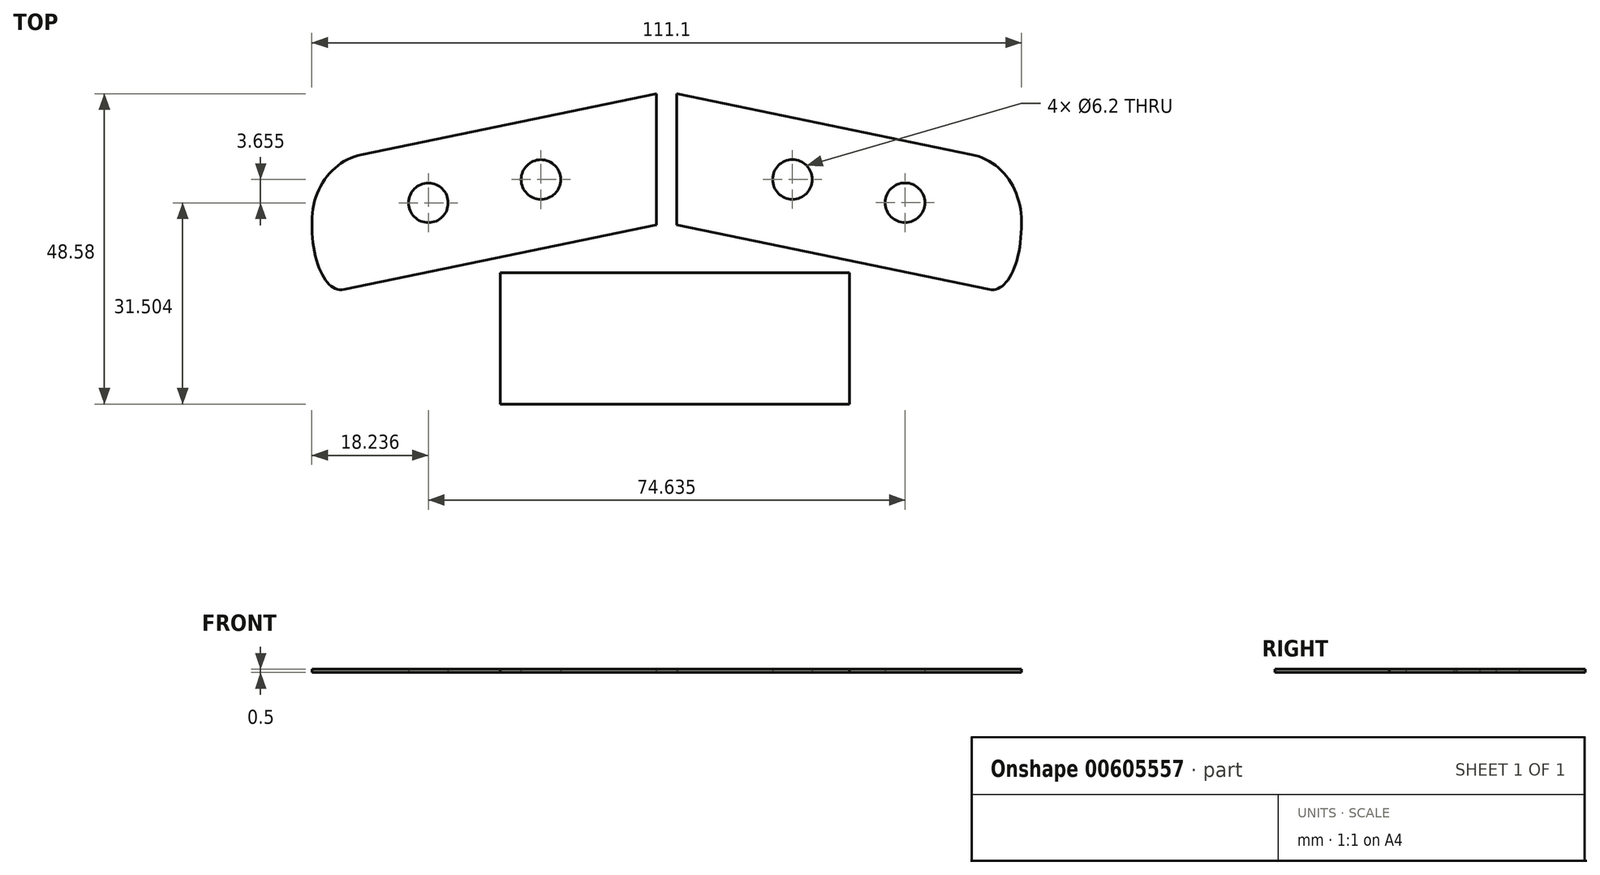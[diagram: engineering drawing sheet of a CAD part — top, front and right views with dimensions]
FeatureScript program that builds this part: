
annotation { "Feature Type Name" : "Feature", "Feature Type Description" : "" }
export const myFeature = defineFeature(function(context is Context, id is Id, definition is map)
    precondition{}
    {
        {
            var Q0;
            Q0=qCreatedBy(makeId("Top.planeOp"),FACE);
            var sketch = newSketch(context, id + "F0", { "sketchPlane" : qUnion([Q0])});
            skLineSegment(sketch, "E0.0", {"start": v(-43.66, 1.52) * mm, "end": v(-43.66, 22.05) * mm});
            skLineSegment(sketch, "E0.1", {"start": v(-43.66, 1.52) * mm, "end": v(11, 1.52) * mm});
            skLineSegment(sketch, "E0.2", {"start": v(-43.66, 22.05) * mm, "end": v(11, 22.05) * mm});
            skLineSegment(sketch, "E0.3", {"start": v(11, 22.05) * mm, "end": v(11, 1.52) * mm});
            skLineSegment(sketch, "E1.0", {"start": v(-16, 50.1) * mm, "end": v(-16, 29.57) * mm});
            skLineSegment(sketch, "E1.1", {"start": v(32.93, 19.46) * mm, "end": v(-16, 29.57) * mm});
            skLineSegment(sketch, "E1.2", {"start": v(30.16, 40.58) * mm, "end": v(-15.93, 50.1) * mm});
            skCircle(sketch, "E1.3", {"center": v(2.1, 36.68) * mm, "radius": 3.1 * mm});
            skCircle(sketch, "E1.4", {"center": v(19.72, 33.04) * mm, "radius": 3.1 * mm});
            skEllipticalArc(sketch, "E1.5", {});
            skEllipticalArc(sketch, "E1.6", {});
            skLineSegment(sketch, "E1.7", {"start": v(37.95, 30.13) * mm, "end": v(37.95, 29.84) * mm});
            skLineSegment(sketch, "E2.0", {"start": v(-16, 50.1) * mm, "end": v(-15.93, 50.1) * mm});
            skLineSegment(sketch, "E3.0", {"start": v(-19.2, 29.55) * mm, "end": v(-19.2, 50.08) * mm});
            skLineSegment(sketch, "E3.1", {"start": v(-68.12, 19.45) * mm, "end": v(-19.2, 29.55) * mm});
            skCircle(sketch, "E3.2", {"center": v(-54.91, 33.02) * mm, "radius": 3.1 * mm});
            skCircle(sketch, "E3.3", {"center": v(-37.29, 36.66) * mm, "radius": 3.1 * mm});
            skLineSegment(sketch, "E3.4", {"start": v(-65.36, 40.57) * mm, "end": v(-19.27, 50.09) * mm});
            skLineSegment(sketch, "E3.5", {"start": v(-19.27, 50.09) * mm, "end": v(-19.2, 50.08) * mm});
            skEllipticalArc(sketch, "E3.6", {});
            skEllipticalArc(sketch, "E3.7", {});
            skLineSegment(sketch, "E3.8", {"start": v(-73.15, 30.11) * mm, "end": v(-73.15, 29.83) * mm});
            const initialGuessF0  = {"E1.5": [0.03292744071812428, 0.030879444010317995, -0.04895262450957913, 0.9988011015981232, 0.011474428753066477, 0.005, 3.0295878582004208, 4.600384184987563], "E1.6": [0.02790194554591465, 0.029633939155095018, 0.2022282773088944, 0.9793384113046302, 0.011180339887498943, 0.01, 4.939281783143953, 0], "E3.6": [-0.06309490990535518, 0.029619057740934936, -0.20222827730889414, 0.9793384113046303, 0.011180339887498943, 0.01, 0, 1.343903524035634], "E3.7": [-0.06812040507756481, 0.030864562596157767, -0.048952624509578754, -0.9988011015981231, 0.01147442875306648, 0.005, 4.8243937757811715, 0.11200479537014071]};
            skSetInitialGuess(sketch, initialGuessF0);
            skSolve(sketch);
        }
        {
            var Q0;
            Q0 = qSketchRegion(id + "F0", true);
            extrude(context, id + "F1", {"entities" : qUnion([Q0]), "depth" : .5 * mm, "offsetDistance" : 25 * mm});
        }
    });
